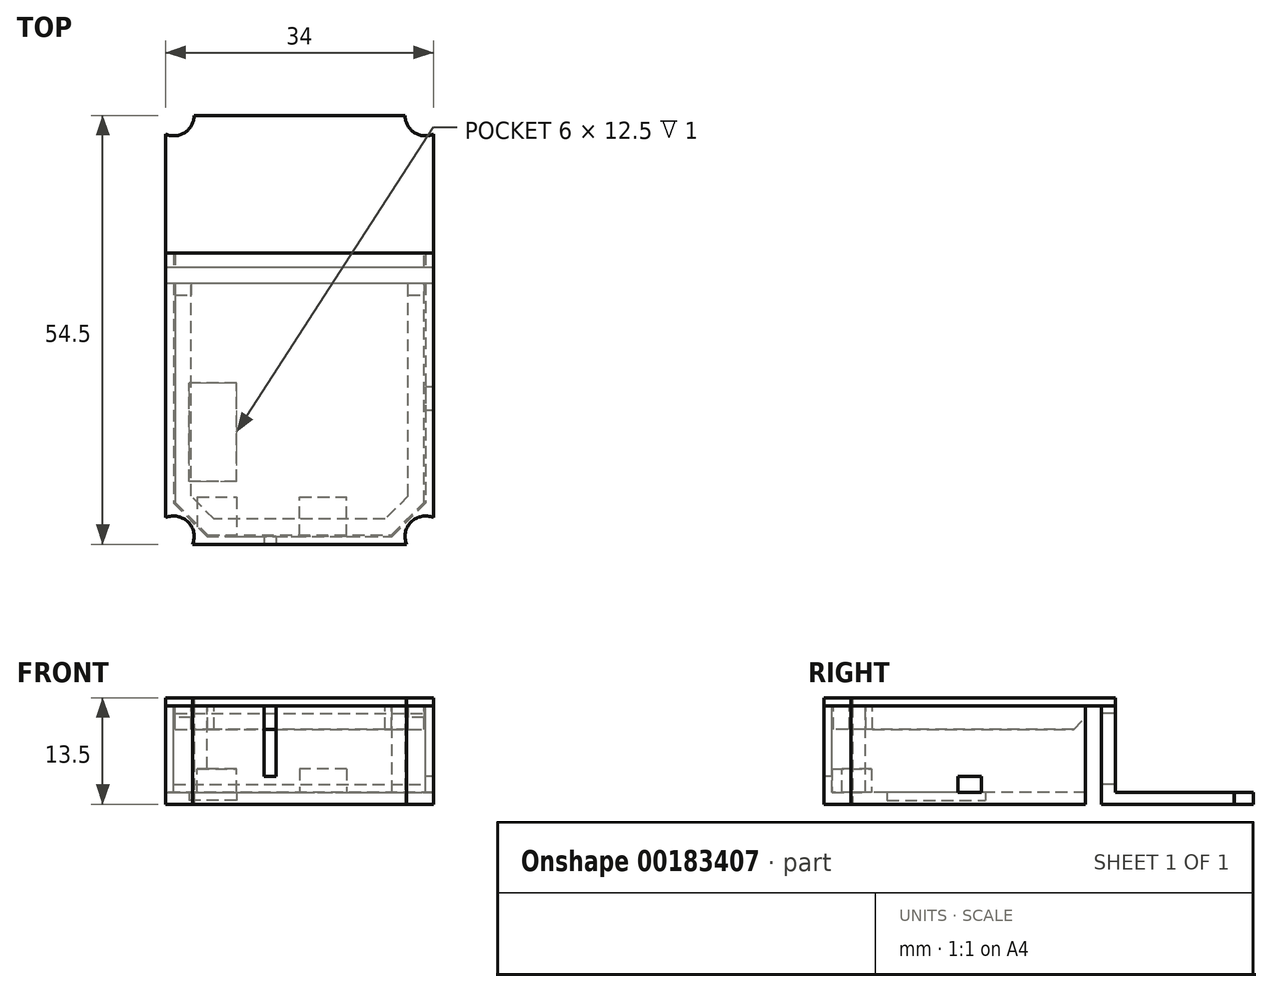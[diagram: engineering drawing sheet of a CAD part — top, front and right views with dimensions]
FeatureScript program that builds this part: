
annotation { "Feature Type Name" : "Feature", "Feature Type Description" : "" }
export const myFeature = defineFeature(function(context is Context, id is Id, definition is map)
    precondition{}
    {
        {
            var Q0;
            Q0=qCreatedBy(makeId("Top.planeOp"),FACE);
            var sketch = newSketch(context, id + "F0", { "sketchPlane" : qUnion([Q0])});
            skLineSegment(sketch, "E0.bottom", {"start": v(-16, 26.75) * mm, "end": v(16, 26.75) * mm, "construction": true});
            skLineSegment(sketch, "E0.top", {"start": v(-16, -26.75) * mm, "end": v(16, -26.75) * mm, "construction": true});
            skLineSegment(sketch, "E0.left", {"start": v(-16, 26.75) * mm, "end": v(-16, -26.75) * mm, "construction": true});
            skLineSegment(sketch, "E0.right", {"start": v(16, 26.75) * mm, "end": v(16, -26.75) * mm, "construction": true});
            skCircle(sketch, "E1", {"center": v(-16, 26.75) * mm, "radius": 1.5 * mm});
            skCircle(sketch, "E2", {"center": v(16, 26.75) * mm, "radius": 1.5 * mm});
            skCircle(sketch, "E3", {"center": v(16, -26.75) * mm, "radius": 1.5 * mm});
            skCircle(sketch, "E4", {"center": v(-16, -26.75) * mm, "radius": 1.5 * mm});
            skPoint(sketch, "E5", {"position": v(0, 26.75) * mm});
            skPoint(sketch, "E6", {"position": v(16, 0) * mm});
            skSolve(sketch);
        }
        {
            var Q0;
            Q0=qCreatedBy(makeId("Top.planeOp"),FACE);
            var sketch = newSketch(context, id + "F1", { "sketchPlane" : qUnion([Q0])});
            skLineSegment(sketch, "E7", {"start": v(-17, 24.35) * mm, "end": v(-17, -24.35) * mm});
            skLineSegment(sketch, "E8", {"start": v(17, -24.35) * mm, "end": v(17, 24.35) * mm});
            skLineSegment(sketch, "E9", {"start": v(13.4, 26.75) * mm, "end": v(-13.4, 26.75) * mm});
            skCircle(sketch, "E10", {"center": v(-16, 26.75) * mm, "radius": 2.6 * mm, "construction": true});
            skCircle(sketch, "E11", {"center": v(16, 26.75) * mm, "radius": 2.6 * mm, "construction": true});
            skCircle(sketch, "E12", {"center": v(16, -26.75) * mm, "radius": 2.6 * mm, "construction": true});
            skCircle(sketch, "E13", {"center": v(-16, -26.75) * mm, "radius": 2.6 * mm, "construction": true});
            skArc(sketch, "E14", {"start": v(-17, 24.35) * mm, "mid": v(-14.56, 24.59) * mm, "end": v(-13.4, 26.75) * mm});
            skArc(sketch, "E15", {"start": v(13.4, 26.75) * mm, "mid": v(14.56, 24.59) * mm, "end": v(17, 24.35) * mm});
            skArc(sketch, "E16", {"start": v(17, -24.35) * mm, "mid": v(14.16, -24.91) * mm, "end": v(13.6, -27.75) * mm});
            skArc(sketch, "E17", {"start": v(-13.6, -27.75) * mm, "mid": v(-14.16, -24.91) * mm, "end": v(-17, -24.35) * mm});
            skLineSegment(sketch, "E18", {"start": v(-13.6, -27.75) * mm, "end": v(13.6, -27.75) * mm});
            skLineSegment(sketch, "E19.bottom", {"start": v(-14, -7.25) * mm, "end": v(-8, -7.25) * mm});
            skLineSegment(sketch, "E19.top", {"start": v(-14, -19.75) * mm, "end": v(-8, -19.75) * mm});
            skLineSegment(sketch, "E19.left", {"start": v(-14, -7.25) * mm, "end": v(-14, -19.75) * mm});
            skLineSegment(sketch, "E19.right", {"start": v(-8, -7.25) * mm, "end": v(-8, -19.75) * mm});
            skSolve(sketch);
        }
        {
            var Q0;
            Q0 = qSketchRegion(id + "F1", true);
            extrude(context, id + "F2", {"entities" : qUnion([Q0]), "depth" : 12.5 * mm});
        }
        {
            var Q0;
            Q0=makeQuery(id+"F2.opExtrude","CAP_FACE",FACE,{"disambiguationData":[OSD([sQuery(id+"F1.wireOp",EDGE,"E7"),sQuery(id+"F1.wireOp",EDGE,"nnypmKSB-atMr-yb57-BFiu-jqMX8Y5RNbDf"),sQuery(id+"F1.wireOp",EDGE,"E8"),sQuery(id+"F1.wireOp",EDGE,"E9"),sQuery(id+"F1.wireOp",EDGE,"E14"),sQuery(id+"F1.wireOp",EDGE,"E15"),sQuery(id+"F1.wireOp",EDGE,"E16"),sQuery(id+"F1.wireOp",EDGE,"E17")])],"isStart":false});
            var sketch = newSketch(context, id + "F3", { "sketchPlane" : qUnion([Q0])});
            skLineSegment(sketch, "E20.left", {"start": v(-16, 9.25) * mm, "end": v(-16, -22.5) * mm});
            skLineSegment(sketch, "E20.right", {"start": v(16, 9.25) * mm, "end": v(16, -22.5) * mm});
            skLineSegment(sketch, "E21", {"start": v(-16, -22.5) * mm, "end": v(-11.76, -26.75) * mm});
            skLineSegment(sketch, "E22", {"start": v(-11.76, -26.75) * mm, "end": v(11.76, -26.75) * mm});
            skLineSegment(sketch, "E23", {"start": v(11.76, -26.75) * mm, "end": v(16, -22.5) * mm});
            skLineSegment(sketch, "E24", {"start": v(-16, 9.25) * mm, "end": v(-17, 9.25) * mm});
            skLineSegment(sketch, "E25", {"start": v(-17, 9.25) * mm, "end": v(-17, 26.75) * mm});
            skLineSegment(sketch, "E26", {"start": v(-17, 26.75) * mm, "end": v(17, 26.75) * mm});
            skLineSegment(sketch, "E27", {"start": v(17, 26.75) * mm, "end": v(17, 9.25) * mm});
            skLineSegment(sketch, "E28", {"start": v(17, 9.25) * mm, "end": v(16, 9.25) * mm});
            skSolve(sketch);
        }
        {
            var Q0;
            Q0 = qSketchRegion(id + "F3", true);
            extrude(context, id + "F4", {"entities" : qUnion([Q0]), "operationType" : NewBodyOperationType.REMOVE, "oppositeDirection" : true, "depth" : 11 * mm});
        }
        {
            var Q0;
            Q0=makeQuery(id+"F4.boolean.opBoolean","COPY",FACE,{"derivedFrom":makeQuery(id+"F4.opExtrude","CAP_FACE",FACE,{"disambiguationData":[OSD([sQuery(id+"F3.wireOp",EDGE,"E20.left"),sQuery(id+"F3.wireOp",EDGE,"E20.right"),sQuery(id+"F3.wireOp",EDGE,"E21"),sQuery(id+"F3.wireOp",EDGE,"E22"),sQuery(id+"F3.wireOp",EDGE,"E23"),sQuery(id+"F3.wireOp",EDGE,"E24"),sQuery(id+"F3.wireOp",EDGE,"E25"),sQuery(id+"F3.wireOp",EDGE,"E26"),sQuery(id+"F3.wireOp",EDGE,"E27"),sQuery(id+"F3.wireOp",EDGE,"E28")])],"isStart":false})});
            var sketch = newSketch(context, id + "F5", { "sketchPlane" : qUnion([Q0])});
            skLineSegment(sketch, "E29.bottom", {"start": v(0, -27.75) * mm, "end": v(6, -27.75) * mm});
            skLineSegment(sketch, "E29.top", {"start": v(0, -21.75) * mm, "end": v(6, -21.75) * mm});
            skLineSegment(sketch, "E29.left", {"start": v(0, -27.75) * mm, "end": v(0, -21.75) * mm});
            skLineSegment(sketch, "E29.right", {"start": v(6, -27.75) * mm, "end": v(6, -21.75) * mm});
            skLineSegment(sketch, "E30.bottom", {"start": v(-13, -21.75) * mm, "end": v(-8, -21.75) * mm});
            skLineSegment(sketch, "E30.top", {"start": v(-13, -27.75) * mm, "end": v(-8, -27.75) * mm});
            skLineSegment(sketch, "E30.left", {"start": v(-13, -21.75) * mm, "end": v(-13, -27.75) * mm});
            skLineSegment(sketch, "E30.right", {"start": v(-8, -21.75) * mm, "end": v(-8, -27.75) * mm});
            skSolve(sketch);
        }
        {
            var Q0;
            Q0 = qSketchRegion(id + "F5", true);
            extrude(context, id + "F6", {"entities" : qUnion([Q0]), "operationType" : NewBodyOperationType.ADD, "depth" : 3 * mm});
        }
        {
            var Q0;
            Q0=makeQuery(id+"F4.boolean.opBoolean","COPY",FACE,{"derivedFrom":makeQuery(id+"F4.opExtrude","CAP_FACE",FACE,{"disambiguationData":[OSD([sQuery(id+"F3.wireOp",EDGE,"E20.left"),sQuery(id+"F3.wireOp",EDGE,"E20.right"),sQuery(id+"F3.wireOp",EDGE,"E21"),sQuery(id+"F3.wireOp",EDGE,"E22"),sQuery(id+"F3.wireOp",EDGE,"E23"),sQuery(id+"F3.wireOp",EDGE,"E24"),sQuery(id+"F3.wireOp",EDGE,"E25"),sQuery(id+"F3.wireOp",EDGE,"E26"),sQuery(id+"F3.wireOp",EDGE,"E27"),sQuery(id+"F3.wireOp",EDGE,"E28")])],"isStart":false})});
            var sketch = newSketch(context, id + "F7", { "sketchPlane" : qUnion([Q0])});
            skLineSegment(sketch, "E31.bottom", {"start": v(-16, 9.25) * mm, "end": v(16, 9.25) * mm});
            skLineSegment(sketch, "E31.top", {"start": v(-16, 7.45) * mm, "end": v(16, 7.45) * mm});
            skLineSegment(sketch, "E31.left", {"start": v(-16, 9.25) * mm, "end": v(-16, 7.45) * mm});
            skLineSegment(sketch, "E31.right", {"start": v(16, 9.25) * mm, "end": v(16, 7.45) * mm});
            skSolve(sketch);
        }
        {
            var Q0;
            Q0 = qSketchRegion(id + "F7", true);
            extrude(context, id + "F8", {"entities" : qUnion([Q0]), "operationType" : NewBodyOperationType.ADD, "depth" : 1 * mm});
        }
        {
            var Q0;
            Q0=makeQuery(id+"F2.opExtrude","CAP_FACE",FACE,{"disambiguationData":[OSD([sQuery(id+"F1.wireOp",EDGE,"E7"),sQuery(id+"F1.wireOp",EDGE,"E8"),sQuery(id+"F1.wireOp",EDGE,"E9"),sQuery(id+"F1.wireOp",EDGE,"E14"),sQuery(id+"F1.wireOp",EDGE,"E15"),sQuery(id+"F1.wireOp",EDGE,"E16"),sQuery(id+"F1.wireOp",EDGE,"E17"),sQuery(id+"F1.wireOp",EDGE,"E18")])],"isStart":false});
            var sketch = newSketch(context, id + "F9", { "sketchPlane" : qUnion([Q0])});
            skLineSegment(sketch, "E32", {"start": v(-17, 9.25) * mm, "end": v(17, 9.25) * mm});
            skLineSegment(sketch, "E33", {"start": v(17, 9.25) * mm, "end": v(17, -24.35) * mm});
            skLineSegment(sketch, "E34", {"start": v(13.6, -27.75) * mm, "end": v(-13.6, -27.75) * mm});
            skLineSegment(sketch, "E35", {"start": v(-17, -24.35) * mm, "end": v(-17, 9.25) * mm});
            skArc(sketch, "E36", {"start": v(-13.6, -27.75) * mm, "mid": v(-14.16, -24.91) * mm, "end": v(-17, -24.35) * mm});
            skArc(sketch, "E37", {"start": v(17, -24.35) * mm, "mid": v(14.16, -24.91) * mm, "end": v(13.6, -27.75) * mm});
            skSolve(sketch);
        }
        {
            var Q0;
            Q0 = qSketchRegion(id + "F9", true);
            extrude(context, id + "F10", {"entities" : qUnion([Q0]), "depth" : 1 * mm});
        }
        {
            var Q0;
            Q0=makeQuery(id+"F3.imprint","IMPRINT",FACE,{"disambiguationData":[TD([[makeQuery(id+"F3.imprint","IMPRINT",EDGE,{"derivedFrom":sQuery(id+"F3.wireOp",EDGE,"E20.left")}),-1.0]])]});
            var sketch = newSketch(context, id + "F11", { "sketchPlane" : qUnion([Q0])});
            skLineSegment(sketch, "E38", {"start": v(-15.8, 9.25) * mm, "end": v(-15.8, -22.42) * mm});
            skLineSegment(sketch, "E39", {"start": v(-15.8, -22.42) * mm, "end": v(-11.67, -26.55) * mm});
            skLineSegment(sketch, "E40", {"start": v(-11.67, -26.55) * mm, "end": v(11.67, -26.55) * mm});
            skLineSegment(sketch, "E41", {"start": v(11.67, -26.55) * mm, "end": v(15.8, -22.42) * mm});
            skLineSegment(sketch, "E42", {"start": v(15.8, -22.42) * mm, "end": v(15.8, 9.25) * mm});
            skLineSegment(sketch, "E43", {"start": v(15.8, 9.25) * mm, "end": v(-15.8, 9.25) * mm});
            skLineSegment(sketch, "E44", {"start": v(13.8, -21.6) * mm, "end": v(10.85, -24.55) * mm});
            skLineSegment(sketch, "E45", {"start": v(10.85, -24.55) * mm, "end": v(-10.85, -24.55) * mm});
            skLineSegment(sketch, "E46", {"start": v(-10.85, -24.55) * mm, "end": v(-13.8, -21.6) * mm});
            skLineSegment(sketch, "E47", {"start": v(-13.8, -21.6) * mm, "end": v(-13.8, 7.45) * mm});
            skLineSegment(sketch, "E48", {"start": v(-13.8, 7.45) * mm, "end": v(13.8, 7.45) * mm});
            skLineSegment(sketch, "E49", {"start": v(13.8, -21.6) * mm, "end": v(13.8, 7.45) * mm});
            skSolve(sketch);
        }
        {
            var Q0;
            Q0 = qSketchRegion(id + "F11", true);
            extrude(context, id + "F12", {"entities" : qUnion([Q0]), "operationType" : NewBodyOperationType.ADD, "oppositeDirection" : true, "depth" : 1 * mm});
        }
        {
            var Q0;
            Q0=makeQuery(id+"F2.opExtrude","SWEPT_FACE",FACE,{"disambiguationData":[OSD([sQuery(id+"F1.wireOp",EDGE,"E18")])]});
            var sketch = newSketch(context, id + "F13", { "sketchPlane" : qUnion([Q0])});
            skLineSegment(sketch, "E50.bottom", {"start": v(-4.5, 12.5) * mm, "end": v(-3, 12.5) * mm});
            skLineSegment(sketch, "E50.top", {"start": v(-4.5, 3.5) * mm, "end": v(-3, 3.5) * mm});
            skLineSegment(sketch, "E50.left", {"start": v(-4.5, 12.5) * mm, "end": v(-4.5, 3.5) * mm});
            skLineSegment(sketch, "E50.right", {"start": v(-3, 12.5) * mm, "end": v(-3, 3.5) * mm});
            skSolve(sketch);
        }
        {
            var Q0;
            Q0 = qSketchRegion(id + "F13", true);
            var Q1;
            Q1=makeQuery(id+"F4.boolean.opBoolean","COPY",FACE,{"derivedFrom":makeQuery(id+"F4.opExtrude","SWEPT_FACE",FACE,{"disambiguationData":[OSD([sQuery(id+"F3.wireOp",EDGE,"E22")])]})});
            extrude(context, id + "F14", {"entities" : qUnion([Q0]), "operationType" : NewBodyOperationType.REMOVE, "endBound" : BoundingType.UP_TO_SURFACE, "oppositeDirection" : true, "endBoundEntityFace" : qUnion([Q1]), "depth" : 25 * mm});
        }
        {
            var Q0;
            Q0=makeQuery(id+"F12.boolean.opBoolean","SPLIT",FACE,{"disambiguationData":[TD([makeQuery(id+"F12.opExtrude","SWEPT_FACE",FACE,{"disambiguationData":[OSD([sQuery(id+"F11.wireOp",EDGE,"E44")])]})])],"derivedFrom":makeQuery(id+"F10.opExtrude","CAP_FACE",FACE,{"disambiguationData":[OSD([sQuery(id+"F9.wireOp",EDGE,"E32"),sQuery(id+"F9.wireOp",EDGE,"E33"),sQuery(id+"F9.wireOp",EDGE,"E34"),sQuery(id+"F9.wireOp",EDGE,"E35"),sQuery(id+"F9.wireOp",EDGE,"E36"),sQuery(id+"F9.wireOp",EDGE,"E37")])],"isStart":true})});
            var sketch = newSketch(context, id + "F15", { "sketchPlane" : qUnion([Q0])});
            skLineSegment(sketch, "E51.bottom", {"start": v(-17, -7.45) * mm, "end": v(17, -7.45) * mm});
            skLineSegment(sketch, "E51.top", {"start": v(-17, -5.45) * mm, "end": v(17, -5.45) * mm});
            skLineSegment(sketch, "E51.left", {"start": v(-17, -7.45) * mm, "end": v(-17, -5.45) * mm});
            skLineSegment(sketch, "E51.right", {"start": v(17, -7.45) * mm, "end": v(17, -5.45) * mm});
            skSolve(sketch);
        }
        {
            var Q0;
            Q0 = qSketchRegion(id + "F15", true);
            extrude(context, id + "F16", {"entities" : qUnion([Q0]), "operationType" : NewBodyOperationType.REMOVE, "depth" : 25 * mm});
        }
        {
            var Q0;
            {var subQ0=sQuery(id+"F11.wireOp",EDGE,"E47");var subQ1=sQuery(id+"F11.wireOp",EDGE,"E46");var subQ2=sQuery(id+"F11.wireOp",EDGE,"E45");var subQ3=sQuery(id+"F11.wireOp",EDGE,"E42");var subQ4=sQuery(id+"F11.wireOp",EDGE,"E49");var subQ5=sQuery(id+"F11.wireOp",EDGE,"E38");var subQ6=sQuery(id+"F11.wireOp",EDGE,"E44");var subQ7=sQuery(id+"F11.wireOp",EDGE,"E39");var subQ8=sQuery(id+"F11.wireOp",EDGE,"E40");var subQ9=sQuery(id+"F11.wireOp",EDGE,"E41");Q0=makeQuery(id+"F16.boolean.opBoolean","SPLIT",FACE,{"disambiguationData":[TD([makeQuery(id+"F12.opExtrude","SWEPT_FACE",FACE,{"disambiguationData":[OSD([subQ7])]})])],"derivedFrom":makeQuery(id+"F12.opExtrude","CAP_FACE",FACE,{"disambiguationData":[OSD([subQ5,subQ7,subQ8,subQ9,subQ3,sQuery(id+"F11.wireOp",EDGE,"E43"),subQ6,subQ2,subQ1,subQ0,sQuery(id+"F11.wireOp",EDGE,"E48"),subQ4])],"isStart":false})});}
            extrude(context, id + "F17", {"entities" : qUnion([Q0]), "operationType" : NewBodyOperationType.ADD, "depth" : 2 * mm});
        }
        {
            var Q0;
            {var subQ0=sQuery(id+"F15.wireOp",EDGE,"E51.top");var subQ1=sQuery(id+"F11.wireOp",EDGE,"E49");var subQ2=sQuery(id+"F11.wireOp",EDGE,"E48");var subQ3=sQuery(id+"F11.wireOp",EDGE,"E47");var subQ4=sQuery(id+"F11.wireOp",EDGE,"E46");var subQ5=sQuery(id+"F11.wireOp",EDGE,"E45");var subQ6=sQuery(id+"F11.wireOp",EDGE,"E44");var subQ7=sQuery(id+"F11.wireOp",EDGE,"E43");var subQ8=sQuery(id+"F11.wireOp",EDGE,"E42");var subQ9=sQuery(id+"F11.wireOp",EDGE,"E41");var subQ10=sQuery(id+"F11.wireOp",EDGE,"E40");var subQ11=sQuery(id+"F11.wireOp",EDGE,"E39");var subQ12=sQuery(id+"F11.wireOp",EDGE,"E38");Q0=makeQuery(id+"F17.opExtrude","CAP_EDGE",EDGE,{"disambiguationData":[OSD([subQ12,subQ11,subQ10,subQ9,subQ8,subQ7,subQ6,subQ5,subQ4,subQ3,subQ2,subQ1,subQ0]),TDD([makeQuery(id+"F16.boolean.opBoolean","INTERSECT",EDGE,{"disambiguationData":[OD(0.0)],"derivedFrom":[makeQuery(id+"F12.opExtrude","CAP_FACE",FACE,{"disambiguationData":[OSD([subQ12,subQ11,subQ10,subQ9,subQ8,subQ7,subQ6,subQ5,subQ4,subQ3,subQ2,subQ1])],"isStart":false}),makeQuery(id+"F16.opExtrude","SWEPT_FACE",FACE,{"disambiguationData":[OSD([subQ0])]})]})])],"isStart":false});}
            var Q1;
            {var subQ0=sQuery(id+"F15.wireOp",EDGE,"E51.top");var subQ1=sQuery(id+"F11.wireOp",EDGE,"E49");var subQ2=sQuery(id+"F11.wireOp",EDGE,"E48");var subQ3=sQuery(id+"F11.wireOp",EDGE,"E47");var subQ4=sQuery(id+"F11.wireOp",EDGE,"E46");var subQ5=sQuery(id+"F11.wireOp",EDGE,"E45");var subQ6=sQuery(id+"F11.wireOp",EDGE,"E44");var subQ7=sQuery(id+"F11.wireOp",EDGE,"E43");var subQ8=sQuery(id+"F11.wireOp",EDGE,"E42");var subQ9=sQuery(id+"F11.wireOp",EDGE,"E41");var subQ10=sQuery(id+"F11.wireOp",EDGE,"E40");var subQ11=sQuery(id+"F11.wireOp",EDGE,"E39");var subQ12=sQuery(id+"F11.wireOp",EDGE,"E38");Q1=makeQuery(id+"F17.opExtrude","CAP_EDGE",EDGE,{"disambiguationData":[OSD([subQ12,subQ11,subQ10,subQ9,subQ8,subQ7,subQ6,subQ5,subQ4,subQ3,subQ2,subQ1,subQ0]),TDD([makeQuery(id+"F16.boolean.opBoolean","INTERSECT",EDGE,{"disambiguationData":[OD(1.0)],"derivedFrom":[makeQuery(id+"F12.opExtrude","CAP_FACE",FACE,{"disambiguationData":[OSD([subQ12,subQ11,subQ10,subQ9,subQ8,subQ7,subQ6,subQ5,subQ4,subQ3,subQ2,subQ1])],"isStart":false}),makeQuery(id+"F16.opExtrude","SWEPT_FACE",FACE,{"disambiguationData":[OSD([subQ0])]})]})])],"isStart":false});}
            chamfer(context, id + "F18", {"entities" : qUnion([Q0, Q1]), "width" : 1.5 * mm, "tangentPropagation" : true});
        }
        {
            var Q0;
            Q0=makeQuery(id+"F2.opExtrude","CAP_FACE",FACE,{"disambiguationData":[OSD([sQuery(id+"F1.wireOp",EDGE,"E7"),sQuery(id+"F1.wireOp",EDGE,"E8"),sQuery(id+"F1.wireOp",EDGE,"E9"),sQuery(id+"F1.wireOp",EDGE,"E14"),sQuery(id+"F1.wireOp",EDGE,"E15"),sQuery(id+"F1.wireOp",EDGE,"E16"),sQuery(id+"F1.wireOp",EDGE,"E17"),sQuery(id+"F1.wireOp",EDGE,"E18"),sQuery(id+"F1.wireOp",EDGE,"E19.bottom"),sQuery(id+"F1.wireOp",EDGE,"E19.top"),sQuery(id+"F1.wireOp",EDGE,"E19.left"),sQuery(id+"F1.wireOp",EDGE,"E19.right")])],"isStart":true});
            var sketch = newSketch(context, id + "F19", { "sketchPlane" : qUnion([Q0])});
            skLineSegment(sketch, "E52.bottom", {"start": v(-5.07, 22.34) * mm, "end": v(-14.8, 22.34) * mm});
            skLineSegment(sketch, "E52.top", {"start": v(-5.07, 5.1) * mm, "end": v(-14.8, 5.1) * mm});
            skLineSegment(sketch, "E52.left", {"start": v(-5.07, 22.34) * mm, "end": v(-5.07, 5.1) * mm});
            skLineSegment(sketch, "E52.right", {"start": v(-14.8, 22.34) * mm, "end": v(-14.8, 5.1) * mm});
            skSolve(sketch);
        }
        {
            var Q0;
            Q0 = qSketchRegion(id + "F19", true);
            extrude(context, id + "F20", {"entities" : qUnion([Q0]), "operationType" : NewBodyOperationType.ADD, "oppositeDirection" : true, "depth" : 0.5 * mm});
        }
        {
            var Q0;
            Q0=makeQuery(id+"F4.boolean.opBoolean","COPY",FACE,{"derivedFrom":makeQuery(id+"F4.opExtrude","SWEPT_FACE",FACE,{"disambiguationData":[OSD([sQuery(id+"F3.wireOp",EDGE,"E20.right")])]})});
            var sketch = newSketch(context, id + "F21", { "sketchPlane" : qUnion([Q0])});
            skLineSegment(sketch, "E53.bottom", {"start": v(7.75, 1.5) * mm, "end": v(10.75, 1.5) * mm});
            skLineSegment(sketch, "E53.top", {"start": v(7.75, 3.5) * mm, "end": v(10.75, 3.5) * mm});
            skLineSegment(sketch, "E53.left", {"start": v(7.75, 1.5) * mm, "end": v(7.75, 3.5) * mm});
            skLineSegment(sketch, "E53.right", {"start": v(10.75, 1.5) * mm, "end": v(10.75, 3.5) * mm});
            skSolve(sketch);
        }
        {
            var Q0;
            Q0 = qSketchRegion(id + "F21", true);
            var Q1;
            Q1=makeQuery(id+"F2.opExtrude","SWEPT_FACE",FACE,{"disambiguationData":[OSD([sQuery(id+"F1.wireOp",EDGE,"E8")])]});
            extrude(context, id + "F22", {"entities" : qUnion([Q0]), "operationType" : NewBodyOperationType.REMOVE, "endBound" : BoundingType.UP_TO_SURFACE, "oppositeDirection" : true, "endBoundEntityFace" : qUnion([Q1]), "depth" : 25 * mm});
        }
    });
